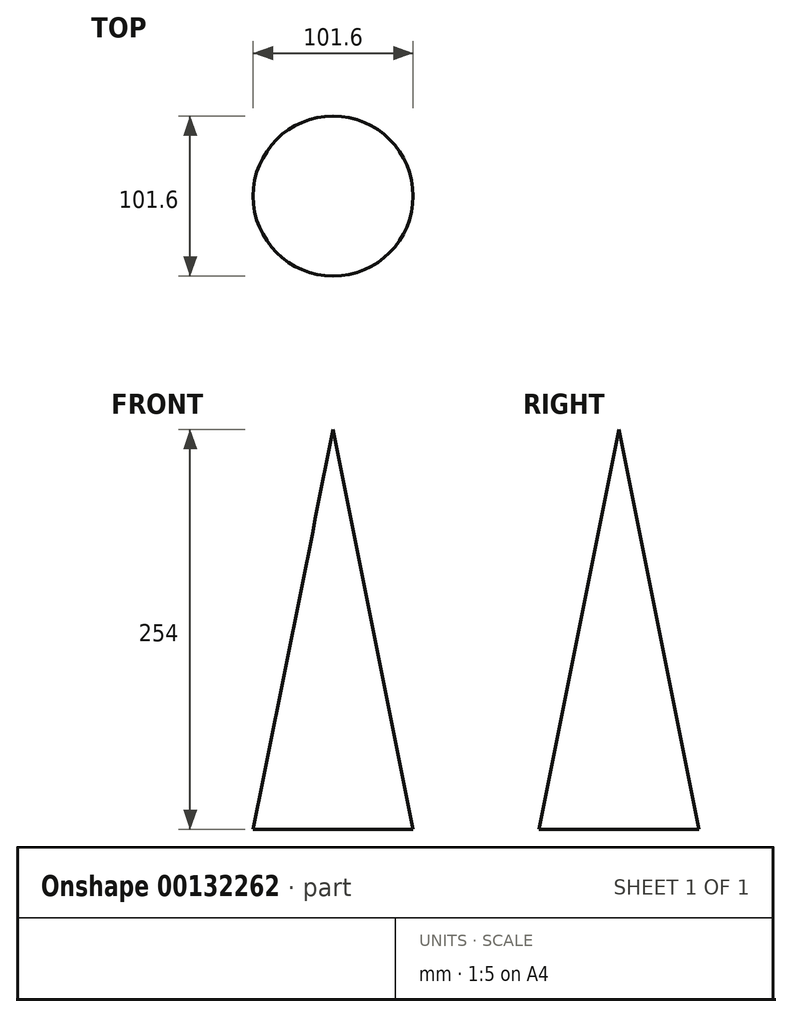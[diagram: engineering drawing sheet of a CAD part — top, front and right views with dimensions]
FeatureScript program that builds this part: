
annotation { "Feature Type Name" : "Feature", "Feature Type Description" : "" }
export const myFeature = defineFeature(function(context is Context, id is Id, definition is map)
    precondition{}
    {
        {
            var Q0;
            Q0=qCreatedBy(makeId("Front.planeOp"),FACE);
            var sketch = newSketch(context, id + "F0", { "sketchPlane" : qUnion([Q0])});
            skLineSegment(sketch, "E0", {"start": v(0, 0) * mm, "end": v(0, 254) * mm});
            skLineSegment(sketch, "E1", {"start": v(0, 254) * mm, "end": v(50.8, 0) * mm});
            skLineSegment(sketch, "E2", {"start": v(50.8, 0) * mm, "end": v(0, 0) * mm});
            skSolve(sketch);
        }
        {
            var Q0;
            Q0 = qSketchRegion(id + "F0", true);
            var Q1;
            Q1=sQuery(id+"F0.wireOp",EDGE,"E0");
            revolve(context, id + "F1", {"entities" : qUnion([Q0]), "axis" : qUnion([Q1]), "revolveType" : RevolveType.FULL});
        }
    });
